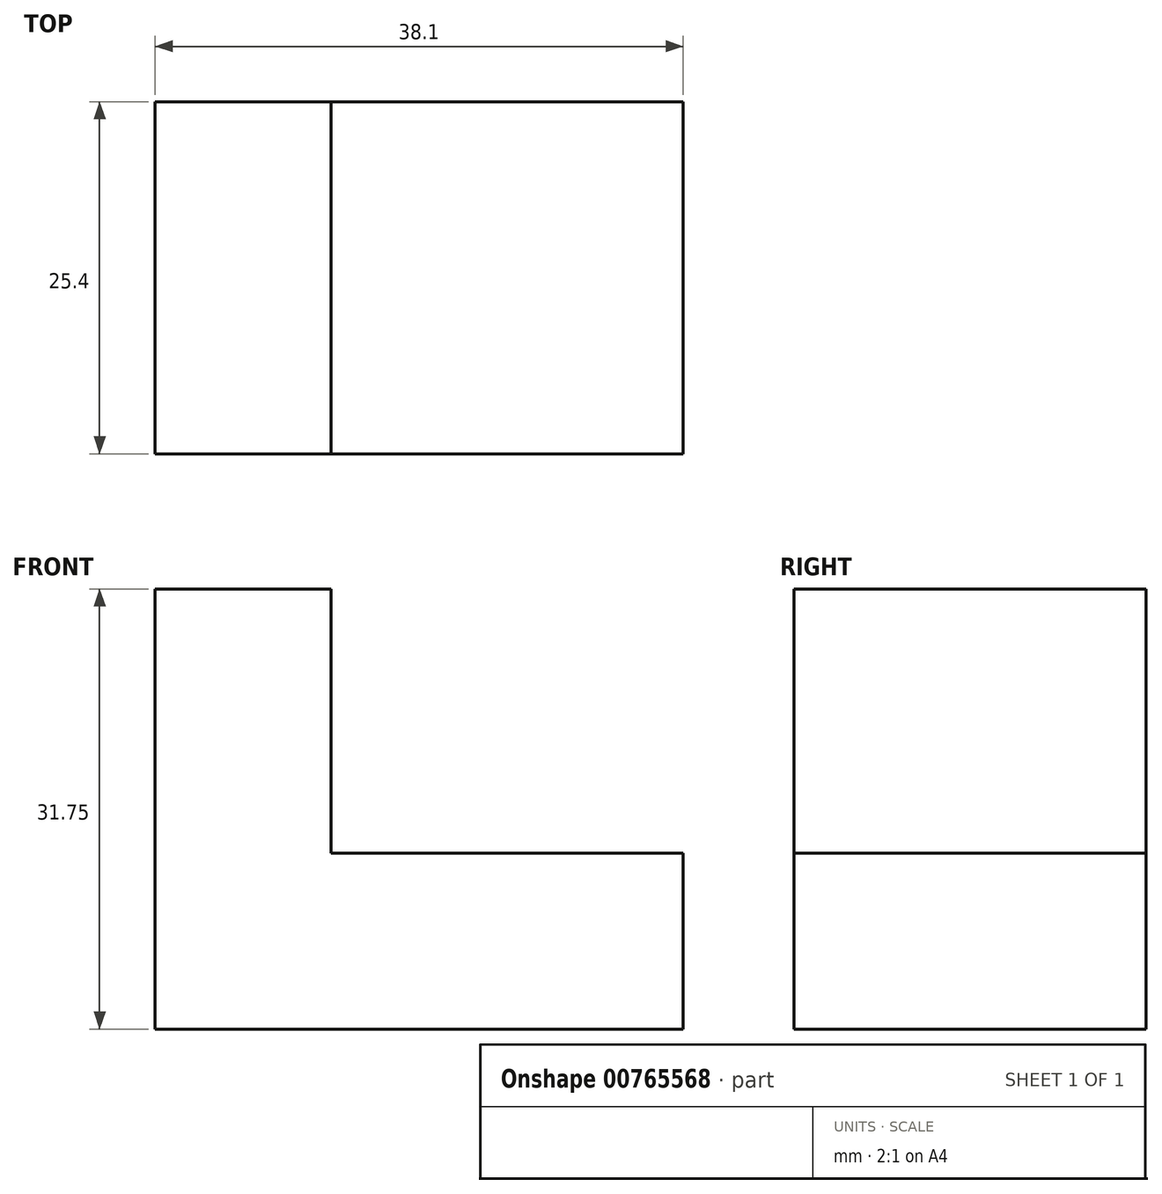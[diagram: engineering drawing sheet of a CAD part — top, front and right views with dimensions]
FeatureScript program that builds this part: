
annotation { "Feature Type Name" : "Feature", "Feature Type Description" : "" }
export const myFeature = defineFeature(function(context is Context, id is Id, definition is map)
    precondition{}
    {
        {
            var Q0;
            Q0=qCreatedBy(makeId("Front.planeOp"),FACE);
            var sketch = newSketch(context, id + "F0", { "sketchPlane" : qUnion([Q0])});
            skLineSegment(sketch, "E0", {"start": v(0, 0) * mm, "end": v(38.1, 0) * mm});
            skLineSegment(sketch, "E1", {"start": v(38.1, 0) * mm, "end": v(38.1, 12.7) * mm});
            skLineSegment(sketch, "E2", {"start": v(38.1, 12.7) * mm, "end": v(12.7, 12.7) * mm});
            skLineSegment(sketch, "E3", {"start": v(12.7, 12.7) * mm, "end": v(12.7, 31.75) * mm});
            skLineSegment(sketch, "E4", {"start": v(0, 31.75) * mm, "end": v(12.7, 31.75) * mm});
            skLineSegment(sketch, "E5", {"start": v(0, 31.75) * mm, "end": v(0, 0) * mm});
            skSolve(sketch);
        }
        {
            var Q0;
            Q0 = qSketchRegion(id + "F0", true);
            extrude(context, id + "F1", {"entities" : qUnion([Q0]), "depth" : 25.4 * mm, "offsetDistance" : 25.4 * mm});
        }
    });
